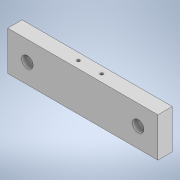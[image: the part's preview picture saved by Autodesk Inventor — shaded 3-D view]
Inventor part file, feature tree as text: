
AUTODESK INVENTOR PART (.ipt)
format: ipt  version: 2021 (Build 250183000, 183)  size: 109,568 bytes
history: native  units: mm
features: extrude x2, sketch x2
ambient origin geometry x8: Origin, YZ Plane, XZ Plane, XY Plane, X Axis, Y Axis, Z Axis, Center Point
bodies: Solid1 (feature_tree)
feature tree (4):
  extrude  "Extrusion1"  Depth=15.5mm
  extrude  "Extrusion2"  Depth=4.0mm
  sketch  "Sketch1"  dims[d0=31.0mm d1=15.5mm]
  sketch  "Sketch2"  dims[d2=5.5mm d3=5.5mm d4=3.2mm d5=4.0mm d6=0.0mm d7=6.5mm d8=3.25mm d9=0.8mm d10=0.0mm d11=0.0mm]
